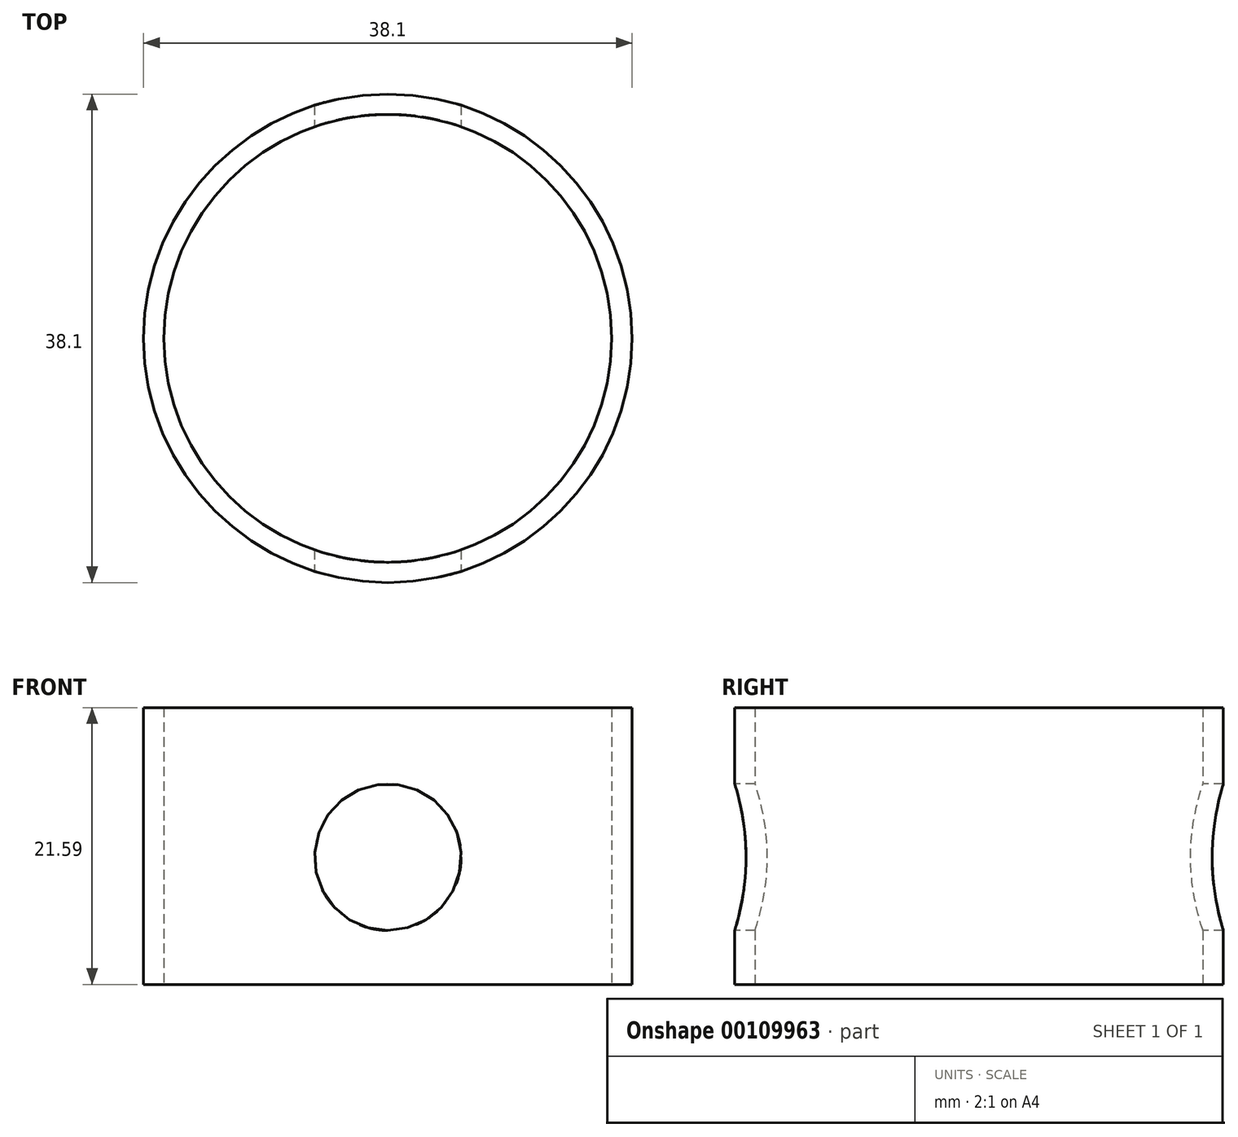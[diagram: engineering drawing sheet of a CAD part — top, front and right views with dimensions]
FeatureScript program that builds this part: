
annotation { "Feature Type Name" : "Feature", "Feature Type Description" : "" }
export const myFeature = defineFeature(function(context is Context, id is Id, definition is map)
    precondition{}
    {
        {
            var Q0;
            Q0=qCreatedBy(makeId("Top.planeOp"),FACE);
            var sketch = newSketch(context, id + "F0", { "sketchPlane" : qUnion([Q0])});
            skCircle(sketch, "E0", {"center": v(0, 0) * mm, "radius": 19.05 * mm});
            skCircle(sketch, "E1.0", {"center": v(0, 0) * mm, "radius": 17.46 * mm});
            skSolve(sketch);
        }
        {
            var Q0;
            Q0=makeQuery(id+"F0.imprint","IMPRINT",FACE,{"disambiguationData":[TD([[makeQuery(id+"F0.imprint","IMPRINT",EDGE,{"derivedFrom":sQuery(id+"F0.wireOp",EDGE,"E0")}),-1.0]])]});
            var Q1;
            Q1=makeQuery(id+"F0.imprint","IMPRINT",FACE,{"disambiguationData":[TD([[makeQuery(id+"F0.imprint","IMPRINT",EDGE,{"derivedFrom":sQuery(id+"F0.wireOp",EDGE,"E0")}),1.0]])]});
            extrude(context, id + "F1", {"entities" : qUnion([Q0, Q1]), "depth" : 21.59 * mm});
        }
        {
            var Q0;
            Q0=qCreatedBy(makeId("Front.planeOp"),FACE);
            var sketch = newSketch(context, id + "F2", { "sketchPlane" : qUnion([Q0])});
            skLineSegment(sketch, "E2", {"start": v(0, 0) * mm, "end": v(0, 19.85) * mm, "construction": true});
            skCircle(sketch, "E3", {"center": v(0, 9.93) * mm, "radius": 5.72 * mm});
            skSolve(sketch);
        }
        {
            var Q0;
            Q0=makeQuery(id+"F2.imprint","IMPRINT",FACE,{"disambiguationData":[TD([[makeQuery(id+"F2.imprint","IMPRINT",EDGE,{"derivedFrom":sQuery(id+"F2.wireOp",EDGE,"E3")}),1.0]])]});
            extrude(context, id + "F3", {"entities" : qUnion([Q0]), "operationType" : NewBodyOperationType.REMOVE, "oppositeDirection" : true, "depth" : 25.4 * mm, "hasSecondDirection" : true, "secondDirectionOppositeDirection" : false, "secondDirectionDepth" : 25.4 * mm});
        }
    });
